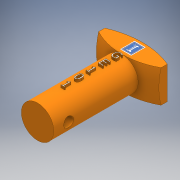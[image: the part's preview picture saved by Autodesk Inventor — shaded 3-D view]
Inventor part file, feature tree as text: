
AUTODESK INVENTOR PART (.ipt)
format: ipt  version: 2018 (Build 220112000, 112)  size: 4,091,904 bytes
history: native  units: mm
features: sketch x7, extrude x4, other x2, revolve x1, emboss x1
ambient origin geometry x8: Origin, YZ Plane, XZ Plane, XY Plane, X Axis, Y Axis, Z Axis, Center Point
bodies: Solid1 (feature_tree)
feature tree (15):
  revolve  "Revolution1"  [1 undecoded]
  extrude  "Extrusion1"  Depth=50.0mm
  extrude  "Extrusion2"  Depth=27.0mm
  extrude  "Extrusion4"  Depth=25.0mm
  extrude  "Extrusion5"  Depth=10.0mm
  other  "Decal1"
  emboss  "Emboss1"
  sketch  "Sketch1"  dims[d0=6.5mm d1=42.0mm]
  sketch  "Sketch2"  dims[d2=32.0mm d3=50.0mm]
  sketch  "Sketch3"  dims[d4=12.5mm d5=27.0mm]
  sketch  "Sketch5"  dims[d6=90.0deg d7=25.0mm]
  sketch  "Sketch6"  dims[d8=10.0mm d9=0.0mm d10=32.0mm]
  sketch  "Sketch7"  dims[d11=32.0mm]
  other  "Image1"
  sketch  "Sketch8"  dims[d12=18.5mm d13=0.0mm d18=13.0mm d19=15.0mm d20=0.0mm d21=6.0mm d22=4.0mm d23=13.0mm d24=0.0mm d50=1.0mm d51=0.0mm]
note: 1 required parameter value undecoded (feature->parameter linkage not recoverable at this tier; creation-order binding heuristic only, values carry confidence <= 0.55)
